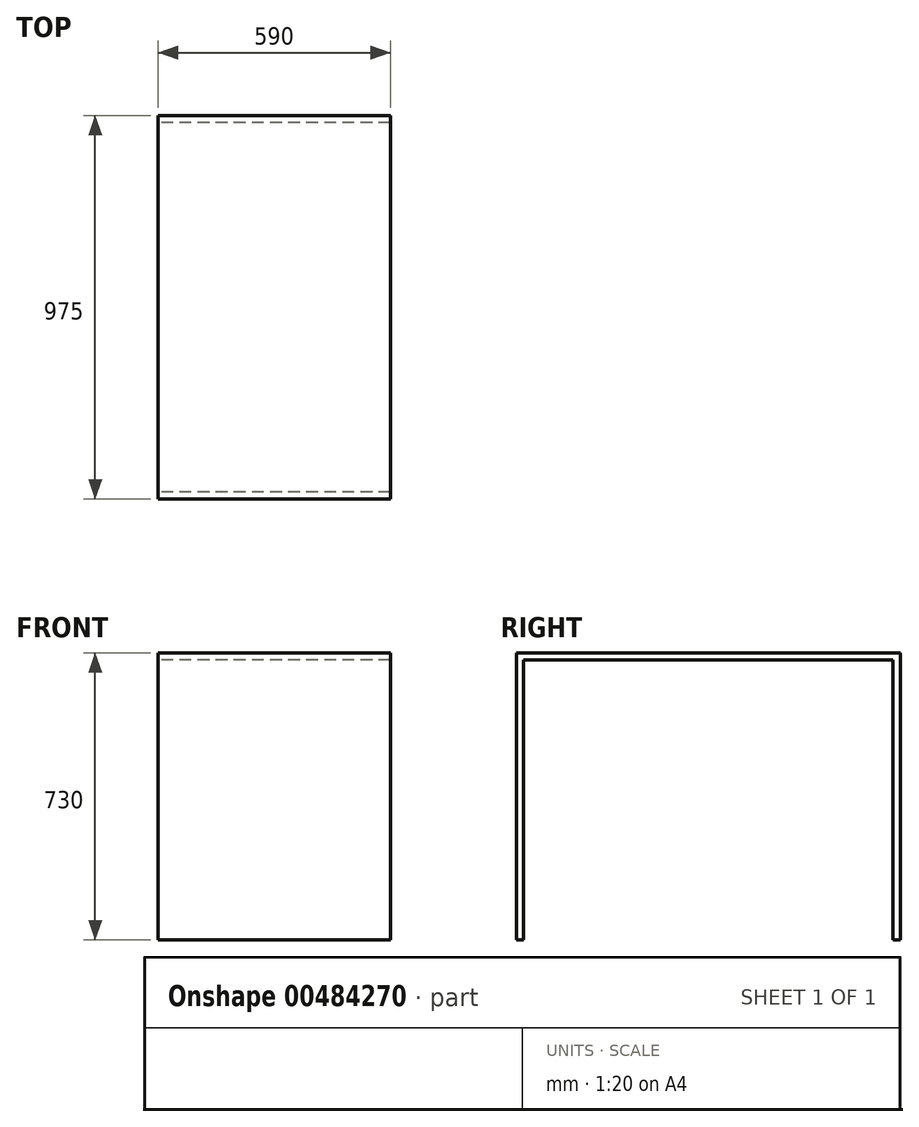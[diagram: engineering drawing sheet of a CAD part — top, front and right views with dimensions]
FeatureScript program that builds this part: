
annotation { "Feature Type Name" : "Feature", "Feature Type Description" : "" }
export const myFeature = defineFeature(function(context is Context, id is Id, definition is map)
    precondition{}
    {
        {
            var Q0;
            Q0=qCreatedBy(makeId("Right.planeOp"),FACE);
            var sketch = newSketch(context, id + "F0", { "sketchPlane" : qUnion([Q0])});
            skLineSegment(sketch, "E0.bottom", {"start": v(0, 0) * mm, "end": v(18, 0) * mm});
            skLineSegment(sketch, "E0.top", {"start": v(0, 730) * mm, "end": v(975, 730) * mm});
            skLineSegment(sketch, "E0.left", {"start": v(0, 0) * mm, "end": v(0, 730) * mm});
            skLineSegment(sketch, "E0.right", {"start": v(975, 0) * mm, "end": v(975, 730) * mm});
            skLineSegment(sketch, "E1", {"start": v(18, 712) * mm, "end": v(18, 0) * mm});
            skLineSegment(sketch, "E2", {"start": v(18, 712) * mm, "end": v(957, 712) * mm});
            skLineSegment(sketch, "E3", {"start": v(957, 712) * mm, "end": v(957, 0) * mm});
            skLineSegment(sketch, "E4.trimOffspring", {"start": v(957, 0) * mm, "end": v(975, 0) * mm});
            skSolve(sketch);
        }
        {
            var Q0;
            Q0=makeQuery(id+"F0.imprint","IMPRINT",FACE,{"disambiguationData":[TD([[makeQuery(id+"F0.imprint","IMPRINT",EDGE,{"derivedFrom":sQuery(id+"F0.wireOp",EDGE,"E0.bottom")}),1.0]])]});
            extrude(context, id + "F1", {"entities" : qUnion([Q0]), "depth" : 590 * mm});
        }
    });
